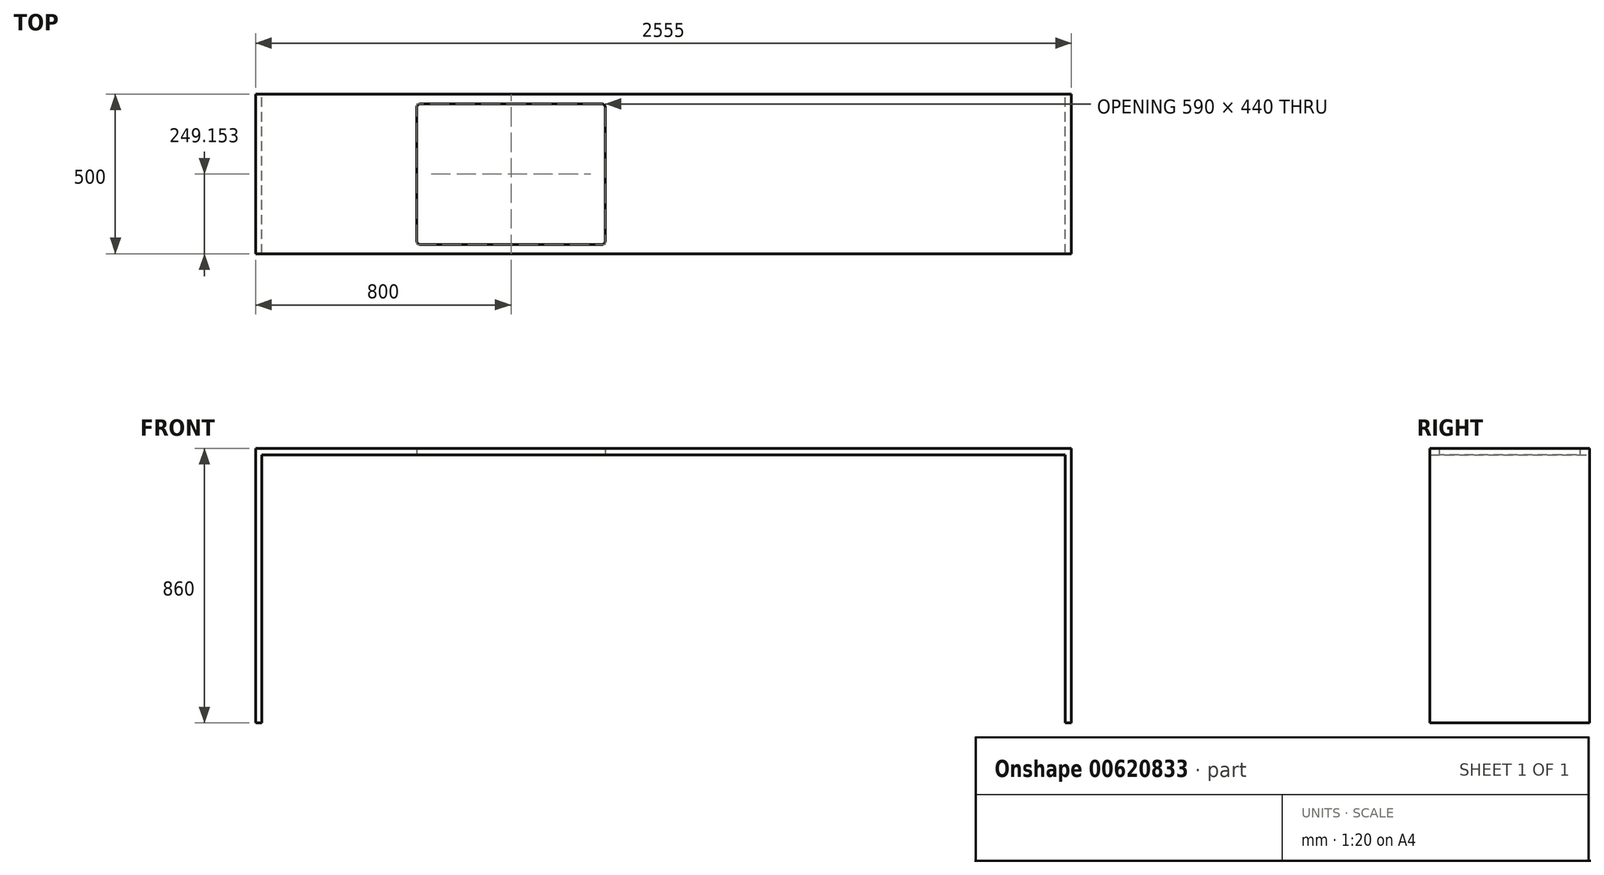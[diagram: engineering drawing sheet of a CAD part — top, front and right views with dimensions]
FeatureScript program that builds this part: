
annotation { "Feature Type Name" : "Feature", "Feature Type Description" : "" }
export const myFeature = defineFeature(function(context is Context, id is Id, definition is map)
    precondition{}
    {
        {
            var Q0;
            Q0=qCreatedBy(makeId("Front.planeOp"),FACE);
            var sketch = newSketch(context, id + "F0", { "sketchPlane" : qUnion([Q0])});
            skLineSegment(sketch, "E0", {"start": v(-2136.34, 0) * mm, "end": v(-2136.34, 840) * mm});
            skLineSegment(sketch, "E1", {"start": v(-2136.34, 840) * mm, "end": v(418.66, 840) * mm});
            skLineSegment(sketch, "E2", {"start": v(418.66, 840) * mm, "end": v(418.66, 0) * mm});
            skLineSegment(sketch, "E3", {"start": v(418.66, 0) * mm, "end": v(398.66, 0) * mm});
            skLineSegment(sketch, "E4", {"start": v(-2136.34, 0) * mm, "end": v(-2116.34, 0) * mm});
            skLineSegment(sketch, "E5", {"start": v(-2116.34, 0) * mm, "end": v(-2116.34, 840) * mm});
            skLineSegment(sketch, "E6", {"start": v(398.66, 0) * mm, "end": v(398.66, 840) * mm});
            skLineSegment(sketch, "E7", {"start": v(-2136.34, 840) * mm, "end": v(-2136.34, 860) * mm});
            skLineSegment(sketch, "E8", {"start": v(-2136.34, 860) * mm, "end": v(418.66, 860) * mm});
            skLineSegment(sketch, "E9", {"start": v(418.66, 860) * mm, "end": v(418.66, 840) * mm});
            skSolve(sketch);
        }
        {
            var Q0;
            Q0 = qSketchRegion(id + "F0", true);
            extrude(context, id + "F1", {"entities" : qUnion([Q0]), "depth" : 500 * mm, "offsetDistance" : 25 * mm});
        }
        {
            var Q0;
            Q0=qCreatedBy(makeId("Top.planeOp"),FACE);
            var sketch = newSketch(context, id + "F2", { "sketchPlane" : qUnion([Q0])});
            skLineSegment(sketch, "E10.bottom", {"start": v(-1051.34, -470.85) * mm, "end": v(-1621.34, -470.85) * mm});
            skLineSegment(sketch, "E10.top", {"start": v(-1051.34, -30.85) * mm, "end": v(-1621.34, -30.85) * mm});
            skLineSegment(sketch, "E10.left", {"start": v(-1041.34, -460.85) * mm, "end": v(-1041.34, -40.85) * mm});
            skLineSegment(sketch, "E10.right", {"start": v(-1631.34, -460.85) * mm, "end": v(-1631.34, -40.85) * mm});
            skPoint(sketch, "E10.middle", {"position": v(-1336.34, -250.85) * mm});
            skPoint(sketch, "E11.visualSharp", {"position": v(-1631.34, -30.85) * mm});
            skArc(sketch, "E11.filletArc", {"start": v(-1621.34, -30.85) * mm, "mid": v(-1628.41, -33.78) * mm, "end": v(-1631.34, -40.85) * mm});
            skPoint(sketch, "E12.visualSharp", {"position": v(-1041.34, -30.85) * mm});
            skArc(sketch, "E12.filletArc", {"start": v(-1041.34, -40.85) * mm, "mid": v(-1044.27, -33.78) * mm, "end": v(-1051.34, -30.85) * mm});
            skPoint(sketch, "E13.visualSharp", {"position": v(-1041.34, -470.85) * mm});
            skArc(sketch, "E13.filletArc", {"start": v(-1051.34, -470.85) * mm, "mid": v(-1044.27, -467.92) * mm, "end": v(-1041.34, -460.85) * mm});
            skPoint(sketch, "E14.visualSharp", {"position": v(-1631.34, -470.85) * mm});
            skArc(sketch, "E14.filletArc", {"start": v(-1631.34, -460.85) * mm, "mid": v(-1628.41, -467.92) * mm, "end": v(-1621.34, -470.85) * mm});
            skSolve(sketch);
        }
        {
            var Q0;
            Q0 = qSketchRegion(id + "F2", true);
            extrude(context, id + "F3", {"entities" : qUnion([Q0]), "operationType" : NewBodyOperationType.REMOVE, "depth" : 1397 * mm, "offsetDistance" : 25 * mm});
        }
    });
